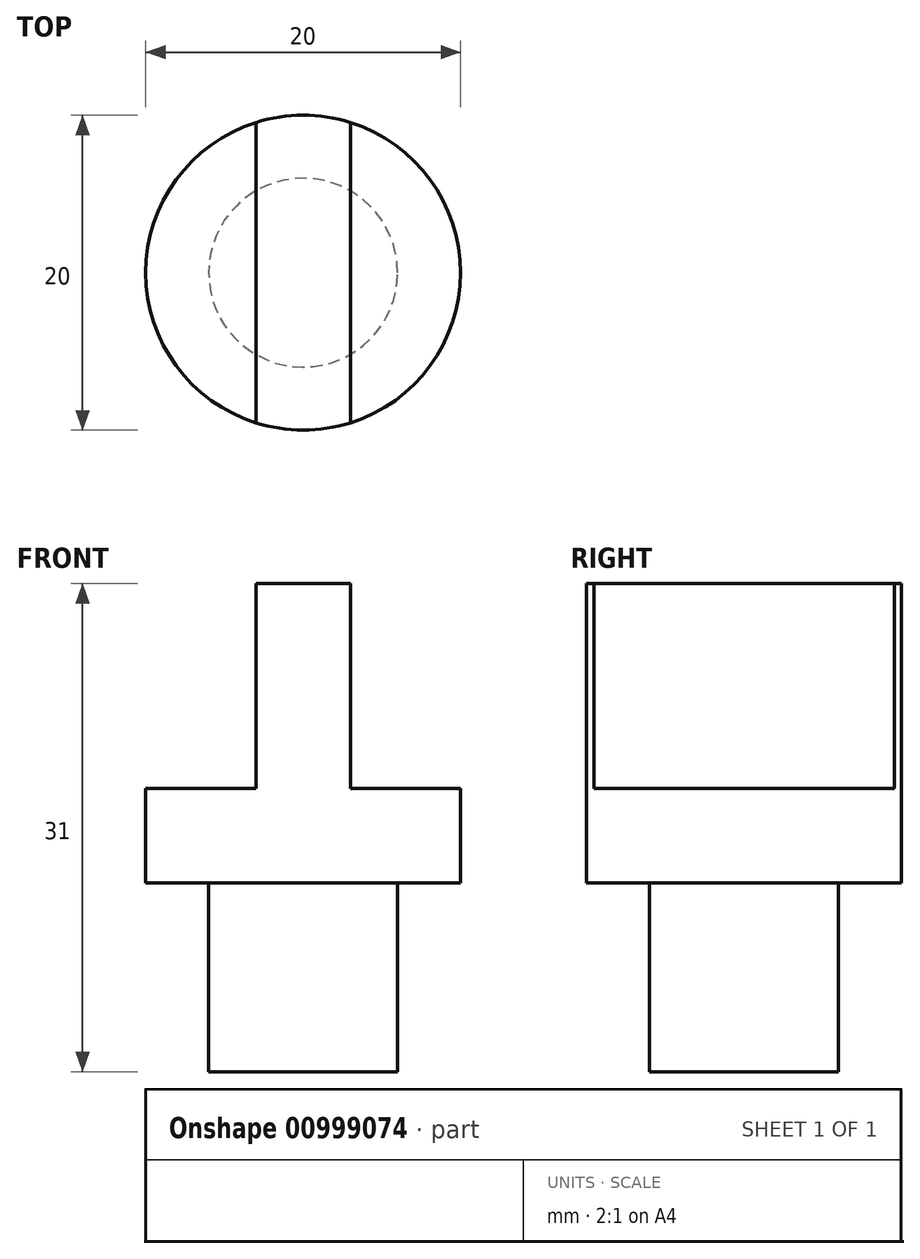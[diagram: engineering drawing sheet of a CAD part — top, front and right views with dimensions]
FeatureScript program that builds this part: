
annotation { "Feature Type Name" : "Feature", "Feature Type Description" : "" }
export const myFeature = defineFeature(function(context is Context, id is Id, definition is map)
    precondition{}
    {
        {
            var Q0;
            Q0=qCreatedBy(makeId("Top.planeOp"),FACE);
            var sketch = newSketch(context, id + "F0", { "sketchPlane" : qUnion([Q0])});
            skCircle(sketch, "E0", {"center": v(0, 0) * mm, "radius": 10 * mm});
            skSolve(sketch);
        }
        {
            var Q0;
            Q0 = qSketchRegion(id + "F0", true);
            extrude(context, id + "F1", {"entities" : qUnion([Q0]), "depth" : 31 * mm, "offsetDistance" : 25 * mm});
        }
        {
            var Q0;
            Q0=makeQuery(id+"F1.opExtrude","CAP_FACE",FACE,{"disambiguationData":[OSD([sQuery(id+"F0.wireOp",EDGE,"E0")])],"isStart":false});
            var sketch = newSketch(context, id + "F2", { "sketchPlane" : qUnion([Q0])});
            skLineSegment(sketch, "E1", {"start": v(0, 0) * mm, "end": v(3, 0) * mm});
            skLineSegment(sketch, "E2", {"start": v(0, 0) * mm, "end": v(-3, 0) * mm});
            skLineSegment(sketch, "E3", {"start": v(-3, 0) * mm, "end": v(-3, 9.54) * mm});
            skLineSegment(sketch, "E4", {"start": v(-3, 9.54) * mm, "end": v(-3, -9.54) * mm});
            skLineSegment(sketch, "E5", {"start": v(3, 0) * mm, "end": v(3, 9.54) * mm});
            skLineSegment(sketch, "E6", {"start": v(3, 9.54) * mm, "end": v(3, -9.54) * mm});
            skSolve(sketch);
        }
        {
            var Q0;
            Q0 = qSketchRegion(id + "F2", true);
            var Q1;
            {var subQ0=sQuery(id+"F2.wireOp",EDGE,"E6");var subQ1=makeQuery(id+"F2.imprint","INTERSECT",VERTEX,{"derivedFrom":[sQuery(id+"F2.wireOp",EDGE,"E1"),subQ0]});Q1=makeQuery(id+"F2.imprint","IMPRINT",FACE,{"disambiguationData":[TD([[makeQuery(id+"F2.imprint","IMPRINT",EDGE,{"disambiguationData":[TD([[subQ1,1.0]])],"derivedFrom":subQ0}),1.0]])]});}
            var Q2;
            {var subQ0=sQuery(id+"F2.wireOp",EDGE,"E4");var subQ1=makeQuery(id+"F2.imprint","INTERSECT",VERTEX,{"derivedFrom":[sQuery(id+"F2.wireOp",EDGE,"E2"),subQ0]});Q2=makeQuery(id+"F2.imprint","IMPRINT",FACE,{"disambiguationData":[TD([[makeQuery(id+"F2.imprint","IMPRINT",EDGE,{"disambiguationData":[TD([[subQ1,1.0]])],"derivedFrom":subQ0}),-1.0]])]});}
            extrude(context, id + "F3", {"entities" : qUnion([Q0, Q1, Q2]), "operationType" : NewBodyOperationType.REMOVE, "oppositeDirection" : true, "depth" : 13 * mm, "offsetDistance" : 25 * mm});
        }
        {
            var Q0;
            Q0=makeQuery(id+"F1.opExtrude","CAP_FACE",FACE,{"disambiguationData":[OSD([sQuery(id+"F0.wireOp",EDGE,"E0")])],"isStart":true});
            var sketch = newSketch(context, id + "F4", { "sketchPlane" : qUnion([Q0])});
            skCircle(sketch, "E7", {"center": v(0, 0) * mm, "radius": 6 * mm});
            skSolve(sketch);
        }
        {
            var Q0;
            Q0=makeQuery(id+"F4.imprint","IMPRINT",FACE,{"disambiguationData":[TD([[makeQuery(id+"F4.imprint","IMPRINT",EDGE,{"derivedFrom":sQuery(id+"F4.wireOp",EDGE,"E7")}),-1.0]])]});
            extrude(context, id + "F5", {"entities" : qUnion([Q0]), "operationType" : NewBodyOperationType.REMOVE, "oppositeDirection" : true, "depth" : 12 * mm, "offsetDistance" : 25 * mm});
        }
    });
